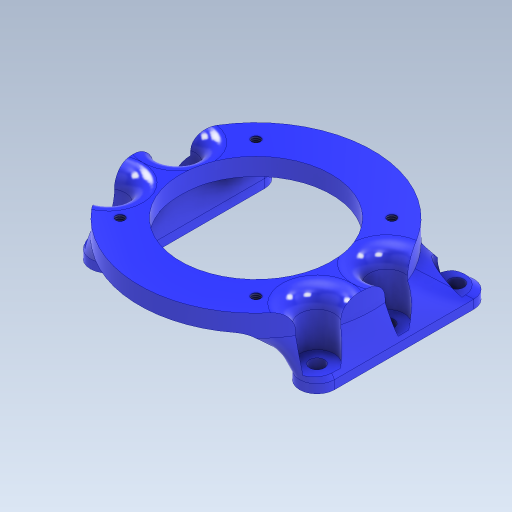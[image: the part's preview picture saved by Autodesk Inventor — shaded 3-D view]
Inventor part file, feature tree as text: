
AUTODESK INVENTOR PART (.ipt)
format: ipt  version: 2023 (Build 270158000, 158)  size: 1,129,472 bytes
history: native  units: in
note: dims shown in document units (in); Inventor stores cm internally (conversion verified against a paired STEP export)
features: sketch x4, other x4, extrude x3, projected_geometry x3, hole x2, loft x2, fillet x2, plane x1
ambient origin geometry x8: Origin, YZ Plane, XZ Plane, XY Plane, X Axis, Y Axis, Z Axis, Center Point
bodies: Solid1 (feature_tree)
feature tree (21):
  sketch  "Sketch1"  dims[d1=1.5748in d2=360.0deg d3=0.1575in d4=0.7232in d5=0.375in d6=0.375in d7=0.5in d8=0.2963in]
  extrude  "Extrusion1"  Depth=0.2963in
  hole  "Hole1"  [1 undecoded]
  plane  "Work Plane1"
  extrude  "Extrusion2"  Depth=0.125in
  extrude  "Extrusion6"  Depth=0.125in TaperAngle=360.0deg
  loft  "Loft1"
  loft  "Loft2"
  hole  "Hole2"  [1 undecoded]
  fillet  "Fillet4"  Radius=0.25in
  fillet  "Fillet5"  Radius=0.5in
  sketch  "Sketch2"  dims[d10=0.25in d11=0.0in]
  sketch  "Sketch7"  dims[d12=0.1276in d13=0.315in d14=0.1654in d15=0.125in d16=0.5635in d17=1.0in d18=0.8108in d19=-0.9471in]
  projected_geometry  "Projected Loop3"
  other  "Edges1"
  other  "Edges2"
  other  "Edges3"
  other  "Edges4"
  sketch  "Sketch8"  dims[d20=3.0in d21=2.0in d22=3.1496in d24=360.0deg d26=0.2087in d27=1.1811in d29=1.0in d30=0.7874in d32=3.0in d35=0.25in d36=0.25in d37=0.5in d38=0.25in d39=0.125in d40=0.0in d58=0.25in d63=0.0625in d64=0.0625in d65=0.0625in d66=0.0in d67=0.0in d68=90.0deg d69=0.0in d70=90.0deg d71=0.0in d72=90.0deg d73=0.0in d74=90.0deg d77=0.2087in d78=1.1811in d80=1.0in d81=0.7874in d83=3.0in d86=0.2126in d87=0.328in d88=0.5in d89=0.75in d90=0.5635in d91=1.0in d92=0.8108in d93=0.375in d94=0.25in d95=0.125in d59=0.0in d60=0.0in d61=0.0in d96=0.0in d97=0.0in d98=0.0in d99=0.0in]
  projected_geometry  "Projected Loop4"
  projected_geometry  "Projected Loop5"
note: 2 required parameter values undecoded (feature->parameter linkage not recoverable at this tier; creation-order binding heuristic only, values carry confidence <= 0.55)
